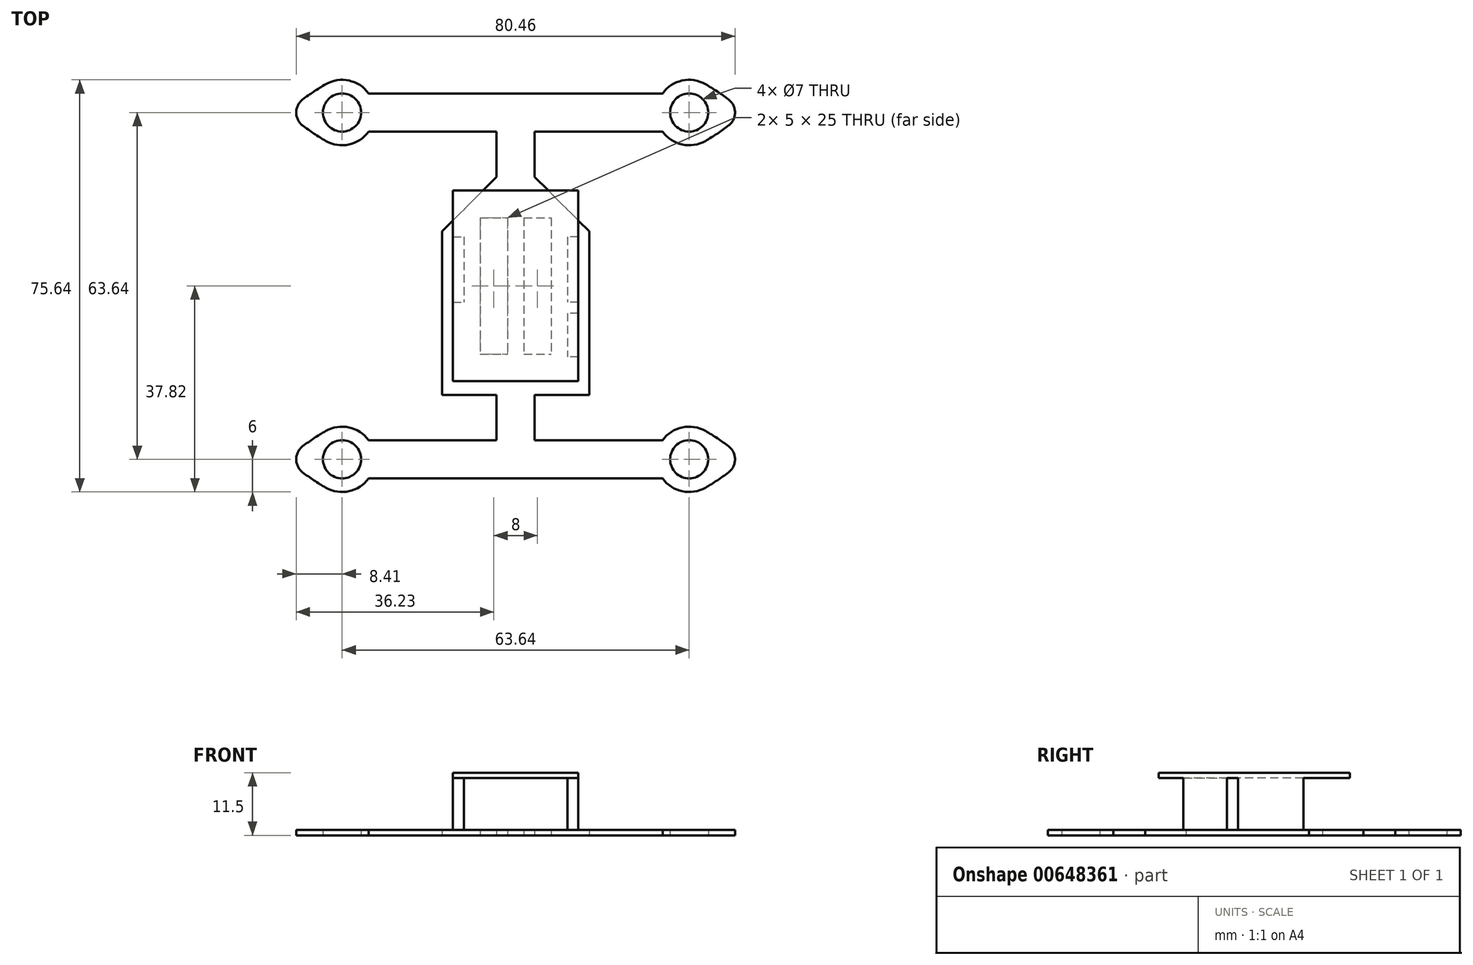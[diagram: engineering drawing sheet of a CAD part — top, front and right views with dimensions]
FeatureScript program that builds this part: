
annotation { "Feature Type Name" : "Feature", "Feature Type Description" : "" }
export const myFeature = defineFeature(function(context is Context, id is Id, definition is map)
    precondition{}
    {
        {
            var Q0;
            Q0=qCreatedBy(makeId("Top.planeOp"),FACE);
            var sketch = newSketch(context, id + "F0", { "sketchPlane" : qUnion([Q0])});
            skLineSegment(sketch, "E0.bottom", {"start": v(31.82, -31.82) * mm, "end": v(-31.82, -31.82) * mm, "construction": true});
            skLineSegment(sketch, "E0.top", {"start": v(31.82, 31.82) * mm, "end": v(-31.82, 31.82) * mm, "construction": true});
            skLineSegment(sketch, "E0.left", {"start": v(31.82, -31.82) * mm, "end": v(31.82, 31.82) * mm, "construction": true});
            skLineSegment(sketch, "E0.right", {"start": v(-31.82, -31.82) * mm, "end": v(-31.82, 31.82) * mm, "construction": true});
            skPoint(sketch, "E0.middle", {"position": v(0, 0) * mm});
            skLineSegment(sketch, "E1.bottom", {"start": v(13.5, -20) * mm, "end": v(3.5, -20) * mm});
            skLineSegment(sketch, "E1.top", {"start": v(13.5, 20) * mm, "end": v(3.5, 20) * mm, "construction": true});
            skLineSegment(sketch, "E1.left", {"start": v(13.5, -20) * mm, "end": v(13.5, 10) * mm});
            skLineSegment(sketch, "E1.right", {"start": v(-13.5, -20) * mm, "end": v(-13.5, 20) * mm, "construction": true});
            skArc(sketch, "E2", {"start": v(-34.82, 26.62) * mm, "mid": v(-30.56, 25.95) * mm, "end": v(-26.95, 28.32) * mm});
            skCircle(sketch, "E3", {"center": v(-31.82, 31.82) * mm, "radius": 3.5 * mm});
            skLineSegment(sketch, "E4", {"start": v(0, 0) * mm, "end": v(0, 51.93) * mm, "construction": true});
            skLineSegment(sketch, "E5", {"start": v(0, 0) * mm, "end": v(65.04, 0) * mm, "construction": true});
            skCircle(sketch, "E6.MirrorC", {"center": v(31.82, 31.82) * mm, "radius": 3.5 * mm});
            skArc(sketch, "E7.MirrorC", {"start": v(26.95, 35.32) * mm, "mid": v(30.56, 37.69) * mm, "end": v(34.82, 37.02) * mm});
            skCircle(sketch, "E8.MirrorC", {"center": v(31.82, -31.82) * mm, "radius": 3.5 * mm});
            skArc(sketch, "E9.MirrorC", {"start": v(26.95, -35.32) * mm, "mid": v(30.56, -37.69) * mm, "end": v(34.82, -37.02) * mm});
            skLineSegment(sketch, "E10", {"start": v(-26.95, 35.32) * mm, "end": v(26.95, 35.32) * mm});
            skLineSegment(sketch, "E11", {"start": v(-26.95, 28.32) * mm, "end": v(-3.5, 28.32) * mm});
            skLineSegment(sketch, "E12", {"start": v(-3.5, 28.32) * mm, "end": v(-3.5, 20) * mm});
            skLineSegment(sketch, "E13", {"start": v(3.5, 20) * mm, "end": v(3.5, 28.32) * mm});
            skLineSegment(sketch, "E14", {"start": v(3.5, 28.32) * mm, "end": v(26.95, 28.32) * mm});
            skLineSegment(sketch, "E15.MirrorCS", {"start": v(3.5, -28.32) * mm, "end": v(26.95, -28.32) * mm});
            skLineSegment(sketch, "E16.MirrorCS", {"start": v(3.5, -20) * mm, "end": v(3.5, -28.32) * mm});
            skLineSegment(sketch, "E17.MirrorCS", {"start": v(-3.5, -28.32) * mm, "end": v(-3.5, -20) * mm});
            skLineSegment(sketch, "E18.MirrorCS", {"start": v(-26.95, -35.32) * mm, "end": v(26.95, -35.32) * mm});
            skLineSegment(sketch, "E19.MirrorCS", {"start": v(-26.95, -28.32) * mm, "end": v(-3.5, -28.32) * mm});
            skArc(sketch, "E20", {"start": v(39.04, 34.2) * mm, "mid": v(36.98, 35.68) * mm, "end": v(34.82, 37.02) * mm});
            skArc(sketch, "E21", {"start": v(34.82, 26.62) * mm, "mid": v(36.98, 27.96) * mm, "end": v(39.04, 29.43) * mm});
            skPoint(sketch, "E22.visualSharp", {"position": v(41.9, 31.82) * mm});
            skArc(sketch, "E22.filletArc", {"start": v(39.04, 29.43) * mm, "mid": v(40.23, 31.82) * mm, "end": v(39.04, 34.2) * mm});
            skArc(sketch, "E23", {"start": v(39.04, -29.43) * mm, "mid": v(36.98, -27.96) * mm, "end": v(34.82, -26.62) * mm});
            skArc(sketch, "E24", {"start": v(34.82, -37.02) * mm, "mid": v(36.98, -35.68) * mm, "end": v(39.04, -34.2) * mm});
            skPoint(sketch, "E25.visualSharp", {"position": v(41.9, -31.82) * mm});
            skArc(sketch, "E25.filletArc", {"start": v(39.04, -34.2) * mm, "mid": v(40.23, -31.82) * mm, "end": v(39.04, -29.43) * mm});
            skArc(sketch, "E26.trimOffspring", {"start": v(34.82, -26.62) * mm, "mid": v(30.56, -25.95) * mm, "end": v(26.95, -28.32) * mm});
            skArc(sketch, "E27.MirrorCS", {"start": v(-39.04, -34.2) * mm, "mid": v(-40.23, -31.82) * mm, "end": v(-39.04, -29.43) * mm});
            skArc(sketch, "E28.MirrorCS", {"start": v(-34.82, -37.02) * mm, "mid": v(-36.98, -35.68) * mm, "end": v(-39.04, -34.2) * mm});
            skArc(sketch, "E29.MirrorCS", {"start": v(-34.82, -26.62) * mm, "mid": v(-30.56, -25.95) * mm, "end": v(-26.95, -28.32) * mm});
            skArc(sketch, "E30.MirrorCS", {"start": v(-26.95, -35.32) * mm, "mid": v(-30.56, -37.69) * mm, "end": v(-34.82, -37.02) * mm});
            skPoint(sketch, "E31.MirrorP", {"position": v(-41.9, -31.82) * mm});
            skCircle(sketch, "E32.MirrorC", {"center": v(-31.82, -31.82) * mm, "radius": 3.5 * mm});
            skArc(sketch, "E33.MirrorCS", {"start": v(-39.04, -29.43) * mm, "mid": v(-36.98, -27.96) * mm, "end": v(-34.82, -26.62) * mm});
            skArc(sketch, "E34", {"start": v(-34.82, 37.02) * mm, "mid": v(-36.98, 35.68) * mm, "end": v(-39.04, 34.2) * mm});
            skArc(sketch, "E35", {"start": v(-39.04, 29.43) * mm, "mid": v(-36.98, 27.96) * mm, "end": v(-34.82, 26.62) * mm});
            skPoint(sketch, "E36.visualSharp", {"position": v(-41.9, 31.82) * mm});
            skArc(sketch, "E36.filletArc", {"start": v(-39.04, 34.2) * mm, "mid": v(-40.23, 31.82) * mm, "end": v(-39.04, 29.43) * mm});
            skArc(sketch, "E37.trimOffspring", {"start": v(-26.95, 35.32) * mm, "mid": v(-30.56, 37.69) * mm, "end": v(-34.82, 37.02) * mm});
            skLineSegment(sketch, "E38.trimOffspring", {"start": v(-3.5, 20) * mm, "end": v(-13.5, 20) * mm, "construction": true});
            skLineSegment(sketch, "E39.trimOffspring", {"start": v(-3.5, -20) * mm, "end": v(-13.5, -20) * mm});
            skArc(sketch, "E40.trimOffspring", {"start": v(34.82, 26.62) * mm, "mid": v(30.56, 25.95) * mm, "end": v(26.95, 28.32) * mm});
            skLineSegment(sketch, "E41.bottom", {"start": v(-6.5, 12.5) * mm, "end": v(-1.5, 12.5) * mm});
            skLineSegment(sketch, "E41.top", {"start": v(-6.5, -12.5) * mm, "end": v(-1.5, -12.5) * mm});
            skLineSegment(sketch, "E41.left", {"start": v(-6.5, 12.5) * mm, "end": v(-6.5, -12.5) * mm});
            skLineSegment(sketch, "E41.right", {"start": v(-1.5, 12.5) * mm, "end": v(-1.5, -12.5) * mm});
            skLineSegment(sketch, "E42.bottom", {"start": v(1.5, 12.5) * mm, "end": v(6.5, 12.5) * mm});
            skLineSegment(sketch, "E42.top", {"start": v(1.5, -12.5) * mm, "end": v(6.5, -12.5) * mm});
            skLineSegment(sketch, "E42.left", {"start": v(1.5, 12.5) * mm, "end": v(1.5, -12.5) * mm});
            skLineSegment(sketch, "E42.right", {"start": v(6.5, 12.5) * mm, "end": v(6.5, -12.5) * mm});
            skLineSegment(sketch, "E43", {"start": v(3.5, 20) * mm, "end": v(13.5, 10) * mm});
            skLineSegment(sketch, "E44", {"start": v(-3.5, 20) * mm, "end": v(-13.5, 10) * mm});
            skLineSegment(sketch, "E45", {"start": v(-13.5, 10) * mm, "end": v(-13.5, -20) * mm});
            skSolve(sketch);
        }
        {
            var Q0;
            Q0=makeQuery(id+"F0.imprint","IMPRINT",FACE,{"disambiguationData":[TD([[makeQuery(id+"F0.imprint","IMPRINT",EDGE,{"derivedFrom":sQuery(id+"F0.wireOp",EDGE,"E1.bottom")}),-1.0]])]});
            extrude(context, id + "F1", {"entities" : qUnion([Q0]), "depth" : 1 * mm, "offsetDistance" : 25 * mm});
        }
        {
            var Q0;
            Q0=makeQuery(id+"F1.opExtrude","CAP_FACE",FACE,{"disambiguationData":[OSD([sQuery(id+"F0.wireOp",EDGE,"E1.bottom"),sQuery(id+"F0.wireOp",EDGE,"E1.left"),sQuery(id+"F0.wireOp",EDGE,"E2"),sQuery(id+"F0.wireOp",EDGE,"E3"),sQuery(id+"F0.wireOp",EDGE,"E6.MirrorC"),sQuery(id+"F0.wireOp",EDGE,"E7.MirrorC"),sQuery(id+"F0.wireOp",EDGE,"E8.MirrorC"),sQuery(id+"F0.wireOp",EDGE,"E9.MirrorC"),sQuery(id+"F0.wireOp",EDGE,"E10"),sQuery(id+"F0.wireOp",EDGE,"E11"),sQuery(id+"F0.wireOp",EDGE,"E12"),sQuery(id+"F0.wireOp",EDGE,"E13"),sQuery(id+"F0.wireOp",EDGE,"E14"),sQuery(id+"F0.wireOp",EDGE,"E15.MirrorCS"),sQuery(id+"F0.wireOp",EDGE,"E16.MirrorCS"),sQuery(id+"F0.wireOp",EDGE,"E17.MirrorCS"),sQuery(id+"F0.wireOp",EDGE,"E18.MirrorCS"),sQuery(id+"F0.wireOp",EDGE,"E19.MirrorCS"),sQuery(id+"F0.wireOp",EDGE,"E20"),sQuery(id+"F0.wireOp",EDGE,"E21"),sQuery(id+"F0.wireOp",EDGE,"E22.filletArc"),sQuery(id+"F0.wireOp",EDGE,"E23"),sQuery(id+"F0.wireOp",EDGE,"E24"),sQuery(id+"F0.wireOp",EDGE,"E25.filletArc"),sQuery(id+"F0.wireOp",EDGE,"E26.trimOffspring"),sQuery(id+"F0.wireOp",EDGE,"E27.MirrorCS"),sQuery(id+"F0.wireOp",EDGE,"E28.MirrorCS"),sQuery(id+"F0.wireOp",EDGE,"E29.MirrorCS"),sQuery(id+"F0.wireOp",EDGE,"E30.MirrorCS"),sQuery(id+"F0.wireOp",EDGE,"E32.MirrorC"),sQuery(id+"F0.wireOp",EDGE,"E33.MirrorCS"),sQuery(id+"F0.wireOp",EDGE,"E34"),sQuery(id+"F0.wireOp",EDGE,"E35"),sQuery(id+"F0.wireOp",EDGE,"E36.filletArc"),sQuery(id+"F0.wireOp",EDGE,"E37.trimOffspring"),sQuery(id+"F0.wireOp",EDGE,"E39.trimOffspring"),sQuery(id+"F0.wireOp",EDGE,"E40.trimOffspring"),sQuery(id+"F0.wireOp",EDGE,"E41.bottom"),sQuery(id+"F0.wireOp",EDGE,"E41.top"),sQuery(id+"F0.wireOp",EDGE,"E41.left"),sQuery(id+"F0.wireOp",EDGE,"E41.right"),sQuery(id+"F0.wireOp",EDGE,"E42.bottom"),sQuery(id+"F0.wireOp",EDGE,"E42.top"),sQuery(id+"F0.wireOp",EDGE,"E42.left"),sQuery(id+"F0.wireOp",EDGE,"E42.right"),sQuery(id+"F0.wireOp",EDGE,"E43"),sQuery(id+"F0.wireOp",EDGE,"E44"),sQuery(id+"F0.wireOp",EDGE,"E45")])],"isStart":false});
            var sketch = newSketch(context, id + "F2", { "sketchPlane" : qUnion([Q0])});
            skLineSegment(sketch, "E46.bottom", {"start": v(11.5, -17.5) * mm, "end": v(-11.5, -17.5) * mm, "construction": true});
            skLineSegment(sketch, "E46.top", {"start": v(11.5, 17.5) * mm, "end": v(-11.5, 17.5) * mm, "construction": true});
            skLineSegment(sketch, "E46.left", {"start": v(11.5, -17.5) * mm, "end": v(11.5, 17.5) * mm, "construction": true});
            skLineSegment(sketch, "E46.right", {"start": v(-11.5, -17.5) * mm, "end": v(-11.5, 17.5) * mm, "construction": true});
            skPoint(sketch, "E46.middle", {"position": v(0, 0) * mm});
            skLineSegment(sketch, "E47", {"start": v(-11.5, 9) * mm, "end": v(11.5, 9) * mm, "construction": true});
            skLineSegment(sketch, "E48.bottom", {"start": v(-11.5, 9) * mm, "end": v(-9.5, 9) * mm});
            skLineSegment(sketch, "E48.top", {"start": v(-11.5, -3) * mm, "end": v(-9.5, -3) * mm});
            skLineSegment(sketch, "E48.left", {"start": v(-11.5, 9) * mm, "end": v(-11.5, -3) * mm});
            skLineSegment(sketch, "E48.right", {"start": v(-9.5, 9) * mm, "end": v(-9.5, -3) * mm});
            skLineSegment(sketch, "E49.bottom", {"start": v(11.5, 9) * mm, "end": v(9.5, 9) * mm});
            skLineSegment(sketch, "E49.top", {"start": v(11.5, -3) * mm, "end": v(9.5, -3) * mm});
            skLineSegment(sketch, "E49.left", {"start": v(11.5, 9) * mm, "end": v(11.5, -3) * mm});
            skLineSegment(sketch, "E49.right", {"start": v(9.5, 9) * mm, "end": v(9.5, -3) * mm});
            skLineSegment(sketch, "E50.bottom", {"start": v(11.5, -5) * mm, "end": v(9.5, -5) * mm});
            skLineSegment(sketch, "E50.top", {"start": v(11.5, -13) * mm, "end": v(9.5, -13) * mm});
            skLineSegment(sketch, "E50.left", {"start": v(11.5, -5) * mm, "end": v(11.5, -13) * mm});
            skLineSegment(sketch, "E50.right", {"start": v(9.5, -5) * mm, "end": v(9.5, -13) * mm});
            skSolve(sketch);
        }
        {
            var Q0;
            Q0 = qSketchRegion(id + "F2", true);
            extrude(context, id + "F3", {"entities" : qUnion([Q0]), "operationType" : NewBodyOperationType.ADD, "depth" : 9.5 * mm, "offsetDistance" : 25 * mm});
        }
        {
            var Q0;
            Q0=makeQuery(id+"F3.opExtrude","CAP_FACE",FACE,{"disambiguationData":[OSD([sQuery(id+"F2.wireOp",EDGE,"E48.bottom"),sQuery(id+"F2.wireOp",EDGE,"E48.top"),sQuery(id+"F2.wireOp",EDGE,"E48.left"),sQuery(id+"F2.wireOp",EDGE,"E48.right")])],"isStart":false});
            var sketch = newSketch(context, id + "F4", { "sketchPlane" : qUnion([Q0])});
            skLineSegment(sketch, "E51.bottom", {"start": v(11.5, -17.5) * mm, "end": v(-11.5, -17.5) * mm});
            skLineSegment(sketch, "E51.top", {"start": v(11.5, 17.5) * mm, "end": v(-11.5, 17.5) * mm});
            skLineSegment(sketch, "E51.left", {"start": v(11.5, -17.5) * mm, "end": v(11.5, 17.5) * mm});
            skLineSegment(sketch, "E51.right", {"start": v(-11.5, -17.5) * mm, "end": v(-11.5, 17.5) * mm});
            skPoint(sketch, "E51.middle", {"position": v(0, 0) * mm});
            skSolve(sketch);
        }
        {
            var Q0;
            Q0 = qSketchRegion(id + "F4", true);
            extrude(context, id + "F5", {"entities" : qUnion([Q0]), "operationType" : NewBodyOperationType.ADD, "depth" : 1 * mm, "offsetDistance" : 25 * mm});
        }
    });
